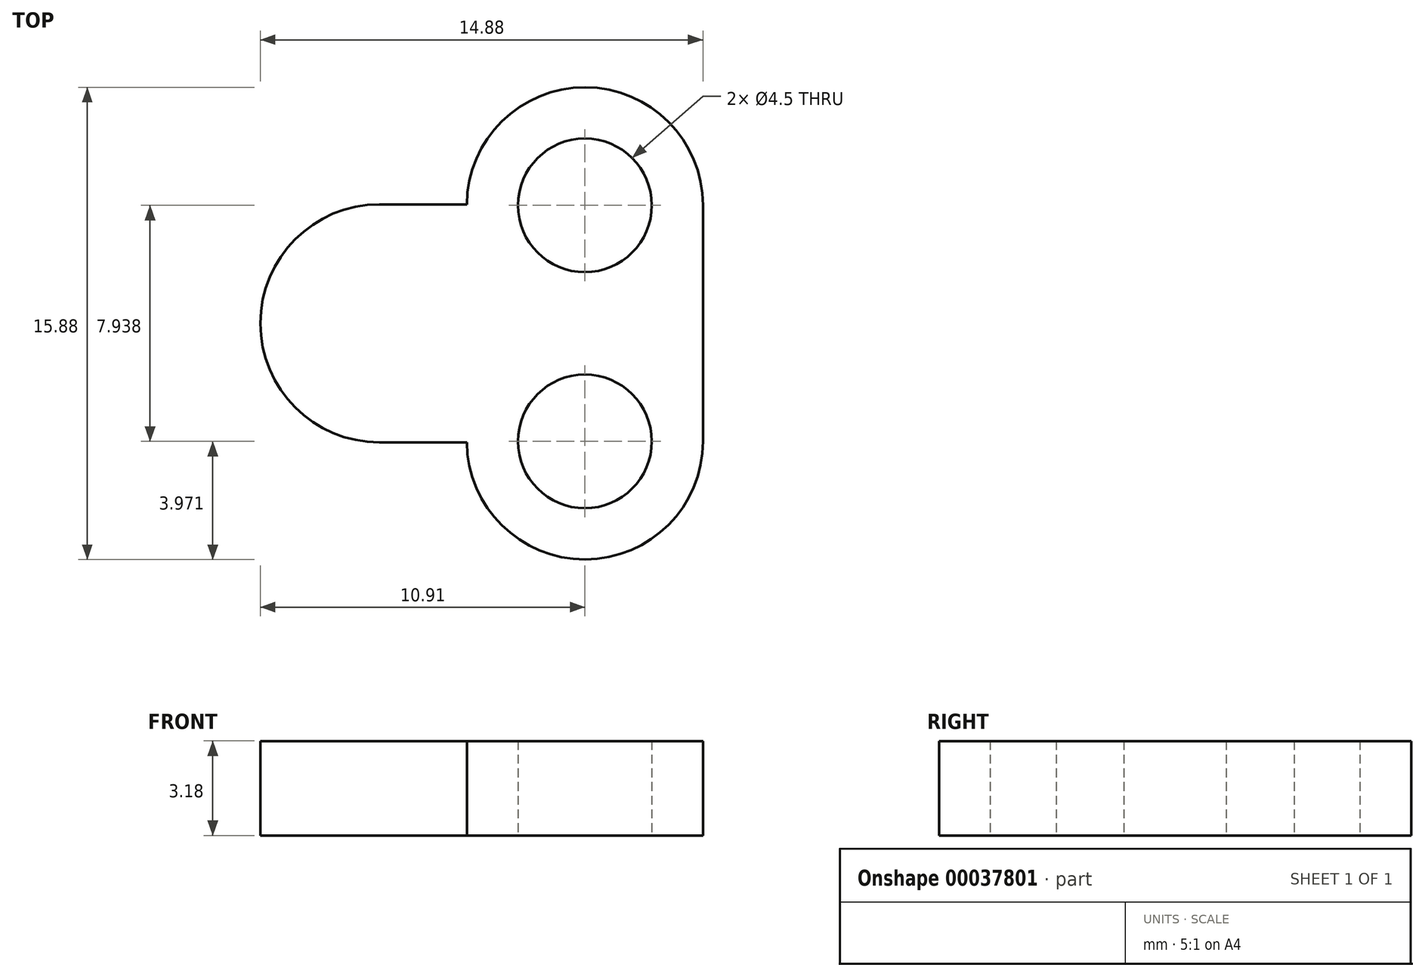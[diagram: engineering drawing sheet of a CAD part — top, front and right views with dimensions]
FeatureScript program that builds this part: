
annotation { "Feature Type Name" : "Feature", "Feature Type Description" : "" }
export const myFeature = defineFeature(function(context is Context, id is Id, definition is map)
    precondition{}
    {
        {
            var Q0;
            Q0=qCreatedBy(makeId("Top.planeOp"),FACE);
            var sketch = newSketch(context, id + "F0", { "sketchPlane" : qUnion([Q0])});
            skLineSegment(sketch, "E0.bottom", {"start": v(0, 0) * mm, "end": v(2.94, 0) * mm});
            skLineSegment(sketch, "E0.top", {"start": v(0, -8) * mm, "end": v(2.94, -8) * mm});
            skLineSegment(sketch, "E0.left", {"start": v(0, 0) * mm, "end": v(0, -8) * mm});
            skArc(sketch, "E1", {"start": v(0, 0) * mm, "mid": v(-4, -4) * mm, "end": v(0, -8) * mm});
            skCircle(sketch, "E2", {"center": v(0, -4) * mm, "radius": 4 * mm, "construction": true});
            skLineSegment(sketch, "E3", {"start": v(0, -4) * mm, "end": v(6.91, -4) * mm, "construction": true});
            skLineSegment(sketch, "E4", {"start": v(6.91, -0.03) * mm, "end": v(6.91, -7.97) * mm, "construction": true});
            skCircle(sketch, "E5", {"center": v(6.91, -0.03) * mm, "radius": 2.25 * mm});
            skCircle(sketch, "E6", {"center": v(6.91, -7.97) * mm, "radius": 2.25 * mm});
            skLineSegment(sketch, "E7", {"start": v(6.91, -4) * mm, "end": v(10.88, -4) * mm, "construction": true});
            skLineSegment(sketch, "E8", {"start": v(10.88, -0.03) * mm, "end": v(10.88, -7.97) * mm});
            skArc(sketch, "E9", {"start": v(2.94, -8) * mm, "mid": v(6.93, -11.94) * mm, "end": v(10.88, -7.97) * mm});
            skArc(sketch, "E10", {"start": v(10.88, -0.03) * mm, "mid": v(6.93, 3.94) * mm, "end": v(2.94, 0) * mm});
            skSolve(sketch);
        }
        {
            var Q0;
            Q0 = qSketchRegion(id + "F0", true);
            extrude(context, id + "F1", {"entities" : qUnion([Q0]), "depth" : 3.17 * mm});
        }
    });
